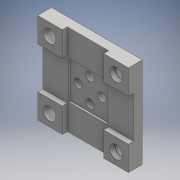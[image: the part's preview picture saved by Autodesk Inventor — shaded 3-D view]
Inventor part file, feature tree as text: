
AUTODESK INVENTOR PART (.ipt)
format: ipt  version: 2016 (Build 200138000, 138)  size: 198,144 bytes
history: native  units: mm
features: sketch x5, extrude x3, hole x2
ambient origin geometry x8: Origin, YZ Plane, XZ Plane, XY Plane, X Axis, Y Axis, Z Axis, Center Point
bodies: Solid1 (feature_tree)
feature tree (10):
  extrude  "Extrusion1"  Depth=46.0mm
  extrude  "Extrusion3"  Depth=1.0mm TaperAngle=0.0deg
  hole  "Hole2"  [1 undecoded]
  hole  "Hole3"  [1 undecoded]
  extrude  "Extrusion4"  Depth=12.5mm
  sketch  "Sketch2"  dims[d0=46.0mm d1=46.0mm]
  sketch  "Sketch6"  dims[d2=3.5mm d3=0.0mm d24=1.0mm d25=0.0mm]
  sketch  "Sketch7"  dims[d26=6.5mm d27=6.0mm]
  sketch  "Sketch8"  dims[d28=6.0mm d29=6.5mm]
  sketch  "Sketch9"  dims[d30=6.0mm d31=6.5mm d32=6.0mm d33=6.5mm d34=6.5mm d35=6.0mm d36=4.0mm d37=2.0mm d38=90.0deg d39=9.0mm d40=0.0mm d41=13.25mm d42=13.25mm d43=13.25mm d44=13.25mm d45=6.0mm d46=6.0mm d47=6.0mm d48=6.0mm d49=4.25mm d50=6.0mm d51=4.25mm d52=6.0mm d53=4.25mm d54=6.0mm d55=4.25mm d56=6.0mm d57=4.25mm d58=6.0mm d59=4.0mm d60=2.0mm d61=90.0deg d62=8.0mm d63=20.594885mm d66=12.5mm d67=12.5mm d68=12.5mm d69=12.5mm d70=12.5mm d71=12.5mm d72=6.5mm d73=6.5mm d74=6.5mm d75=2.5mm d76=0.0mm d77=12.5mm d78=12.5mm]
note: 2 required parameter values undecoded (feature->parameter linkage not recoverable at this tier; creation-order binding heuristic only, values carry confidence <= 0.55)
